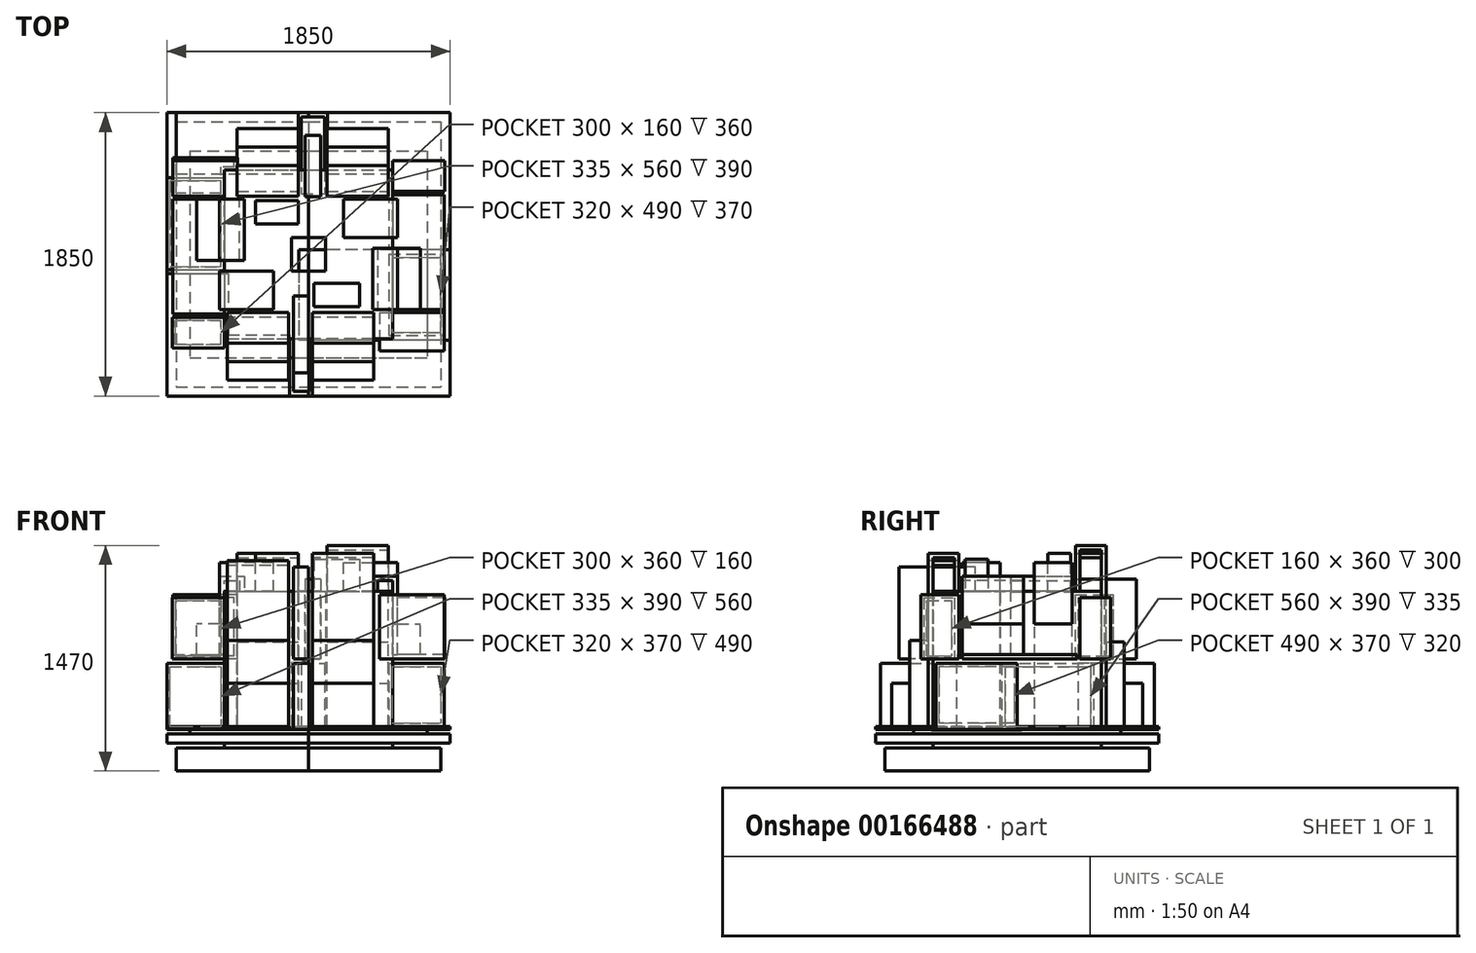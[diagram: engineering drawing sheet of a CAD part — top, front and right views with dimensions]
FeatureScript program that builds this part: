
annotation { "Feature Type Name" : "Feature", "Feature Type Description" : "" }
export const myFeature = defineFeature(function(context is Context, id is Id, definition is map)
    precondition{}
    {
        {
            var Q0;
            Q0=qCreatedBy(makeId("Top.planeOp"),FACE);
            var sketch = newSketch(context, id + "F0", { "sketchPlane" : qUnion([Q0])});
            skLineSegment(sketch, "E0.bottom", {"start": v(-865, 865) * mm, "end": v(865, 865) * mm});
            skLineSegment(sketch, "E0.top", {"start": v(-865, -865) * mm, "end": v(865, -865) * mm});
            skLineSegment(sketch, "E0.left", {"start": v(-865, 865) * mm, "end": v(-865, -865) * mm});
            skLineSegment(sketch, "E0.right", {"start": v(865, 865) * mm, "end": v(865, -865) * mm});
            skPoint(sketch, "E0.middle", {"position": v(0, 0) * mm});
            skSolve(sketch);
        }
        {
            var Q0;
            Q0 = qSketchRegion(id + "F0", true);
            extrude(context, id + "F1", {"entities" : qUnion([Q0]), "depth" : 150 * mm});
        }
        {
            var Q0;
            Q0=makeQuery(id+"F1.opExtrude","CAP_FACE",FACE,{"disambiguationData":[OSD([sQuery(id+"F0.wireOp",EDGE,"E0.bottom"),sQuery(id+"F0.wireOp",EDGE,"E0.top"),sQuery(id+"F0.wireOp",EDGE,"E0.left"),sQuery(id+"F0.wireOp",EDGE,"E0.right")])],"isStart":false});
            var sketch = newSketch(context, id + "F2", { "sketchPlane" : qUnion([Q0])});
            skLineSegment(sketch, "E1.bottom", {"start": v(-550, 550) * mm, "end": v(550, 550) * mm});
            skLineSegment(sketch, "E1.top", {"start": v(-550, -550) * mm, "end": v(550, -550) * mm});
            skLineSegment(sketch, "E1.left", {"start": v(-550, 550) * mm, "end": v(-550, -550) * mm});
            skLineSegment(sketch, "E1.right", {"start": v(550, 550) * mm, "end": v(550, -550) * mm});
            skPoint(sketch, "E1.middle", {"position": v(0, 0) * mm});
            skSolve(sketch);
        }
        {
            var Q0;
            Q0 = qSketchRegion(id + "F2", true);
            extrude(context, id + "F3", {"entities" : qUnion([Q0]), "depth" : 30 * mm});
        }
        {
            var Q0;
            Q0=makeQuery(id+"F3.opExtrude","CAP_FACE",FACE,{"disambiguationData":[OSD([sQuery(id+"F2.wireOp",EDGE,"E1.bottom"),sQuery(id+"F2.wireOp",EDGE,"E1.top"),sQuery(id+"F2.wireOp",EDGE,"E1.left"),sQuery(id+"F2.wireOp",EDGE,"E1.right")])],"isStart":false});
            var sketch = newSketch(context, id + "F4", { "sketchPlane" : qUnion([Q0])});
            skLineSegment(sketch, "E2.bottom", {"start": v(-925, 925) * mm, "end": v(925, 925) * mm});
            skLineSegment(sketch, "E2.top", {"start": v(-925, -925) * mm, "end": v(925, -925) * mm});
            skLineSegment(sketch, "E2.left", {"start": v(-925, 925) * mm, "end": v(-925, -925) * mm});
            skLineSegment(sketch, "E2.right", {"start": v(925, 925) * mm, "end": v(925, -925) * mm});
            skPoint(sketch, "E2.middle", {"position": v(0, 0) * mm});
            skSolve(sketch);
        }
        {
            var Q0;
            Q0 = qSketchRegion(id + "F4", true);
            extrude(context, id + "F5", {"entities" : qUnion([Q0]), "depth" : 60 * mm});
        }
        {
            var Q0;
            Q0=makeQuery(id+"F5.opExtrude","CAP_FACE",FACE,{"disambiguationData":[OSD([sQuery(id+"F4.wireOp",EDGE,"E2.bottom"),sQuery(id+"F4.wireOp",EDGE,"E2.top"),sQuery(id+"F4.wireOp",EDGE,"E2.left"),sQuery(id+"F4.wireOp",EDGE,"E2.right")])],"isStart":false});
            var sketch = newSketch(context, id + "F6", { "sketchPlane" : qUnion([Q0])});
            skLineSegment(sketch, "E3.bottom", {"start": v(-775, 674.89) * mm, "end": v(775, 674.89) * mm});
            skLineSegment(sketch, "E3.top", {"start": v(-775, -674.89) * mm, "end": v(775, -674.89) * mm});
            skLineSegment(sketch, "E3.left", {"start": v(-775, 674.89) * mm, "end": v(-775, -674.89) * mm});
            skLineSegment(sketch, "E3.right", {"start": v(775, 674.89) * mm, "end": v(775, -674.89) * mm});
            skPoint(sketch, "E3.middle", {"position": v(0, 0) * mm});
            skSolve(sketch);
        }
        {
            var Q0;
            Q0=makeQuery(id+"F6.imprint","IMPRINT",FACE,{"disambiguationData":[TD([[makeQuery(id+"F6.imprint","IMPRINT",EDGE,{"derivedFrom":sQuery(id+"F6.wireOp",EDGE,"E3.bottom")}),-1.0]])]});
            extrude(context, id + "F7", {"entities" : qUnion([Q0]), "depth" : 30 * mm});
        }
        {
            var Q0;
            Q0=makeQuery(id+"F7.opExtrude","CAP_FACE",FACE,{"disambiguationData":[OSD([sQuery(id+"F6.wireOp",EDGE,"E3.bottom"),sQuery(id+"F6.wireOp",EDGE,"E3.top"),sQuery(id+"F6.wireOp",EDGE,"E3.left"),sQuery(id+"F6.wireOp",EDGE,"E3.right")])],"isStart":false});
            var sketch = newSketch(context, id + "F8", { "sketchPlane" : qUnion([Q0])});
            skLineSegment(sketch, "E4.0", {"start": v(-925, -125) * mm, "end": v(-925, -925) * mm});
            skLineSegment(sketch, "E4.1", {"start": v(-925, -925) * mm, "end": v(-125, -925) * mm});
            skLineSegment(sketch, "E4.2", {"start": v(925, 925) * mm, "end": v(925, 25) * mm});
            skLineSegment(sketch, "E4.3", {"start": v(-865, 925) * mm, "end": v(-65, 925) * mm});
            skLineSegment(sketch, "E5", {"start": v(-925, -125) * mm, "end": v(-525, -125) * mm});
            skLineSegment(sketch, "E6", {"start": v(-525, -125) * mm, "end": v(-525, -525) * mm});
            skLineSegment(sketch, "E7", {"start": v(-525, -525) * mm, "end": v(-125, -525) * mm});
            skLineSegment(sketch, "E8", {"start": v(-125, -525) * mm, "end": v(-125, -925) * mm});
            skLineSegment(sketch, "E9", {"start": v(925, -525) * mm, "end": v(25, -525) * mm});
            skLineSegment(sketch, "E10", {"start": v(25, -525) * mm, "end": v(25, -925) * mm});
            skLineSegment(sketch, "E11", {"start": v(-865, 925) * mm, "end": v(-865, 525) * mm});
            skLineSegment(sketch, "E12", {"start": v(-865, 525) * mm, "end": v(-65, 525) * mm});
            skLineSegment(sketch, "E13", {"start": v(-65, 525) * mm, "end": v(-65, 925) * mm});
            skLineSegment(sketch, "E14", {"start": v(125, 925) * mm, "end": v(125, 525) * mm});
            skLineSegment(sketch, "E15", {"start": v(125, 525) * mm, "end": v(525, 525) * mm});
            skLineSegment(sketch, "E16", {"start": v(525, 525) * mm, "end": v(525, 25) * mm});
            skLineSegment(sketch, "E17.trimOffspring", {"start": v(925, -525) * mm, "end": v(925, -925) * mm});
            skLineSegment(sketch, "E18", {"start": v(925, 25) * mm, "end": v(525, 25) * mm});
            skLineSegment(sketch, "E19.trimOffspring", {"start": v(125, 925) * mm, "end": v(925, 925) * mm});
            skPoint(sketch, "E20.orphan", {"position": v(-925, 925) * mm});
            skLineSegment(sketch, "E21.trimOffspring", {"start": v(25, -925) * mm, "end": v(925, -925) * mm});
            skSolve(sketch);
        }
        {
            var Q0;
            Q0 = qSketchRegion(id + "F8", true);
            extrude(context, id + "F9", {"entities" : qUnion([Q0]), "depth" : 20 * mm});
        }
        {
            var Q0;
            Q0=makeQuery(id+"F7.opExtrude","CAP_FACE",FACE,{"disambiguationData":[OSD([sQuery(id+"F6.wireOp",EDGE,"E3.bottom"),sQuery(id+"F6.wireOp",EDGE,"E3.top"),sQuery(id+"F6.wireOp",EDGE,"E3.left"),sQuery(id+"F6.wireOp",EDGE,"E3.right")])],"isStart":false});
            var sketch = newSketch(context, id + "F10", { "sketchPlane" : qUnion([Q0])});
            skLineSegment(sketch, "E22", {"start": v(-49.02, -922.35) * mm, "end": v(-49.02, -892.35) * mm, "construction": true});
            skLineSegment(sketch, "E23", {"start": v(-127.92, -892.35) * mm, "end": v(-97.92, -892.35) * mm, "construction": true});
            skLineSegment(sketch, "E24.bottom", {"start": v(-97.92, -892.35) * mm, "end": v(2.08, -892.35) * mm});
            skLineSegment(sketch, "E24.top", {"start": v(-97.92, -392.35) * mm, "end": v(2.08, -392.35) * mm});
            skLineSegment(sketch, "E24.left", {"start": v(-97.92, -892.35) * mm, "end": v(-97.92, -392.35) * mm});
            skLineSegment(sketch, "E24.right", {"start": v(2.08, -892.35) * mm, "end": v(2.08, -392.35) * mm});
            skLineSegment(sketch, "E25", {"start": v(0, 926.82) * mm, "end": v(0, 896.82) * mm, "construction": true});
            skLineSegment(sketch, "E26", {"start": v(-66.36, 896.82) * mm, "end": v(-46.36, 896.82) * mm});
            skLineSegment(sketch, "E27.bottom", {"start": v(-46.36, 896.82) * mm, "end": v(103.64, 896.82) * mm});
            skLineSegment(sketch, "E27.top", {"start": v(-46.36, 396.82) * mm, "end": v(103.64, 396.82) * mm});
            skLineSegment(sketch, "E27.left", {"start": v(-46.36, 896.82) * mm, "end": v(-46.36, 396.82) * mm});
            skLineSegment(sketch, "E27.right", {"start": v(103.64, 896.82) * mm, "end": v(103.64, 396.82) * mm});
            skLineSegment(sketch, "E28.bottom", {"start": v(-925, -100) * mm, "end": v(-525, -100) * mm});
            skLineSegment(sketch, "E28.top", {"start": v(-925, 500) * mm, "end": v(-525, 500) * mm});
            skLineSegment(sketch, "E28.left", {"start": v(-925, -100) * mm, "end": v(-925, 500) * mm});
            skLineSegment(sketch, "E28.right", {"start": v(-525, -100) * mm, "end": v(-525, 500) * mm});
            skLineSegment(sketch, "E29", {"start": v(-861.36, 547.89) * mm, "end": v(-861.36, 500) * mm, "construction": true});
            skLineSegment(sketch, "E30.bottom", {"start": v(524.84, 0) * mm, "end": v(884.84, 0) * mm});
            skLineSegment(sketch, "E30.top", {"start": v(524.84, -530) * mm, "end": v(884.84, -530) * mm});
            skLineSegment(sketch, "E30.left", {"start": v(524.84, 0) * mm, "end": v(524.84, -530) * mm});
            skLineSegment(sketch, "E30.right", {"start": v(884.84, 0) * mm, "end": v(884.84, -530) * mm});
            skLineSegment(sketch, "E31", {"start": v(524.84, 0) * mm, "end": v(524.84, 30) * mm, "construction": true});
            skLineSegment(sketch, "E32", {"start": v(524.84, -530) * mm, "end": v(524.84, -560) * mm});
            skSolve(sketch);
        }
        {
            var Q0;
            Q0 = qSketchRegion(id + "F10", true);
            extrude(context, id + "F11", {"entities" : qUnion([Q0]), "depth" : 430 * mm});
        }
        {
            var Q0;
            Q0=makeQuery(id+"F7.opExtrude","CAP_FACE",FACE,{"disambiguationData":[OSD([sQuery(id+"F6.wireOp",EDGE,"E3.bottom"),sQuery(id+"F6.wireOp",EDGE,"E3.top"),sQuery(id+"F6.wireOp",EDGE,"E3.left"),sQuery(id+"F6.wireOp",EDGE,"E3.right")])],"isStart":false});
            var sketch = newSketch(context, id + "F12", { "sketchPlane" : qUnion([Q0])});
            skLineSegment(sketch, "E33.bottom", {"start": v(-550, 550) * mm, "end": v(550, 550) * mm});
            skLineSegment(sketch, "E33.top", {"start": v(-550, -550) * mm, "end": v(550, -550) * mm});
            skLineSegment(sketch, "E33.left", {"start": v(-550, 550) * mm, "end": v(-550, -550) * mm});
            skLineSegment(sketch, "E33.right", {"start": v(550, 550) * mm, "end": v(550, -550) * mm});
            skPoint(sketch, "E33.middle", {"position": v(0, 0) * mm});
            skLineSegment(sketch, "E34.bottom", {"start": v(-110, 110) * mm, "end": v(110, 110) * mm});
            skLineSegment(sketch, "E34.top", {"start": v(-110, -110) * mm, "end": v(110, -110) * mm});
            skLineSegment(sketch, "E34.left", {"start": v(-110, 110) * mm, "end": v(-110, -110) * mm});
            skLineSegment(sketch, "E34.right", {"start": v(110, 110) * mm, "end": v(110, -110) * mm});
            skSolve(sketch);
        }
        {
            var Q0;
            Q0 = qSketchRegion(id + "F12", true);
            extrude(context, id + "F13", {"entities" : qUnion([Q0]), "depth" : 900 * mm});
        }
        {
            var Q0;
            Q0=makeQuery(id+"F13.opExtrude","SWEPT_FACE",FACE,{"disambiguationData":[OSD([sQuery(id+"F12.wireOp",EDGE,"E33.left")])]});
            cPlane(context, id + "F14", {"entities" : qUnion([Q0]), "cplaneType" : CPlaneType.OFFSET, "offset" : 20 * mm, "oppositeDirection" : true, "width" : 150 * mm, "height" : 150 * mm});
        }
        {
            var Q0;
            Q0=qCreatedBy(id+"F14.planeOp",FACE);
            var sketch = newSketch(context, id + "F15", { "sketchPlane" : qUnion([Q0])});
            skLineSegment(sketch, "E35.bottom", {"start": v(550, 290) * mm, "end": v(580, 290) * mm});
            skLineSegment(sketch, "E35.top", {"start": v(550, 1370) * mm, "end": v(580, 1370) * mm});
            skLineSegment(sketch, "E35.left", {"start": v(550, 290) * mm, "end": v(550, 1340) * mm});
            skLineSegment(sketch, "E35.right", {"start": v(580, 290) * mm, "end": v(580, 1370) * mm});
            skLineSegment(sketch, "E36.0", {"start": v(125, 290) * mm, "end": v(925, 290) * mm, "construction": true});
            skLineSegment(sketch, "E37.1", {"start": v(550, 1170) * mm, "end": v(550, 270) * mm, "construction": true});
            skLineSegment(sketch, "E38.bottom", {"start": v(550, 1370) * mm, "end": v(380, 1370) * mm});
            skLineSegment(sketch, "E38.top", {"start": v(550, 1340) * mm, "end": v(410, 1340) * mm});
            skLineSegment(sketch, "E38.right", {"start": v(380, 1370) * mm, "end": v(380, 1340) * mm});
            skLineSegment(sketch, "E39.bottom", {"start": v(380, 1370) * mm, "end": v(410, 1370) * mm});
            skLineSegment(sketch, "E39.top", {"start": v(380, 1170) * mm, "end": v(410, 1170) * mm});
            skLineSegment(sketch, "E39.left", {"start": v(380, 1340) * mm, "end": v(380, 1170) * mm});
            skLineSegment(sketch, "E39.right", {"start": v(410, 1340) * mm, "end": v(410, 1170) * mm});
            skLineSegment(sketch, "E40.0.1", {"start": v(550, 270) * mm, "end": v(550, 1170) * mm});
            skLineSegment(sketch, "E41.0.1", {"start": v(550, 270) * mm, "end": v(550, 1170) * mm, "construction": true});
            skSolve(sketch);
        }
        {
            var Q0;
            Q0 = qSketchRegion(id + "F15", true);
            extrude(context, id + "F16", {"entities" : qUnion([Q0]), "oppositeDirection" : true, "depth" : 400 * mm});
        }
        {
            var Q0;
            Q0=makeQuery(id+"F9.opExtrude","SWEPT_FACE",FACE,{"disambiguationData":[OSD([sQuery(id+"F8.wireOp",EDGE,"E10")])]});
            var sketch = newSketch(context, id + "F17", { "sketchPlane" : qUnion([Q0])});
            skLineSegment(sketch, "E42.bottom", {"start": v(380, 1170) * mm, "end": v(410, 1170) * mm});
            skLineSegment(sketch, "E42.left", {"start": v(380, 1170) * mm, "end": v(380, 1420) * mm});
            skLineSegment(sketch, "E43", {"start": v(380, 1420) * mm, "end": v(580, 1420) * mm});
            skLineSegment(sketch, "E44", {"start": v(580, 1420) * mm, "end": v(580, 290) * mm});
            skLineSegment(sketch, "E45.0", {"start": v(550, 1390) * mm, "end": v(550, 290) * mm});
            skLineSegment(sketch, "E45.1", {"start": v(410, 1390) * mm, "end": v(550, 1390) * mm});
            skLineSegment(sketch, "E45.2", {"start": v(410, 1170) * mm, "end": v(410, 1390) * mm});
            skLineSegment(sketch, "E46", {"start": v(580, 290) * mm, "end": v(550, 290) * mm});
            skSolve(sketch);
        }
        {
            var Q0;
            Q0 = qSketchRegion(id + "F17", true);
            extrude(context, id + "F18", {"entities" : qUnion([Q0]), "oppositeDirection" : true, "depth" : 400 * mm});
        }
        {
            var Q0;
            Q0=makeQuery(id+"F13.opExtrude","SWEPT_FACE",FACE,{"disambiguationData":[OSD([sQuery(id+"F12.wireOp",EDGE,"E33.right")])]});
            cPlane(context, id + "F19", {"entities" : qUnion([Q0]), "cplaneType" : CPlaneType.OFFSET, "offset" : 30 * mm, "oppositeDirection" : true, "width" : 150 * mm, "height" : 150 * mm});
        }
        {
            var Q0;
            Q0=qCreatedBy(id+"F19.planeOp",FACE);
            var sketch = newSketch(context, id + "F20", { "sketchPlane" : qUnion([Q0])});
            skLineSegment(sketch, "E47", {"start": v(550, 290) * mm, "end": v(580, 290) * mm});
            skLineSegment(sketch, "E48", {"start": v(580, 290) * mm, "end": v(580, 1470) * mm});
            skLineSegment(sketch, "E49", {"start": v(580, 1470) * mm, "end": v(380, 1470) * mm});
            skLineSegment(sketch, "E50", {"start": v(380, 1470) * mm, "end": v(380, 1170) * mm});
            skLineSegment(sketch, "E51.0", {"start": v(410, 1440) * mm, "end": v(410, 1170) * mm});
            skLineSegment(sketch, "E51.1", {"start": v(550, 1440) * mm, "end": v(410, 1440) * mm});
            skLineSegment(sketch, "E51.2", {"start": v(550, 290) * mm, "end": v(550, 1440) * mm});
            skLineSegment(sketch, "E52", {"start": v(380, 1170) * mm, "end": v(410, 1170) * mm});
            skSolve(sketch);
        }
        {
            var Q0;
            Q0 = qSketchRegion(id + "F20", true);
            var Q1;
            Q1=makeQuery(id+"F9.opExtrude","SWEPT_FACE",FACE,{"disambiguationData":[OSD([sQuery(id+"F8.wireOp",EDGE,"E14")])]});
            extrude(context, id + "F21", {"entities" : qUnion([Q0]), "oppositeDirection" : true, "endBoundEntityFace" : qUnion([Q1]), "depth" : 400 * mm});
        }
        {
            var Q0;
            Q0=makeQuery(id+"F9.opExtrude","SWEPT_FACE",FACE,{"disambiguationData":[OSD([sQuery(id+"F8.wireOp",EDGE,"E13")])]});
            var sketch = newSketch(context, id + "F22", { "sketchPlane" : qUnion([Q0])});
            skLineSegment(sketch, "E53.0.1", {"start": v(550, 290) * mm, "end": v(580, 290) * mm});
            skLineSegment(sketch, "E53.0.2", {"start": v(580, 290) * mm, "end": v(580, 1420) * mm});
            skLineSegment(sketch, "E53.0.4", {"start": v(380, 1420) * mm, "end": v(380, 1170) * mm});
            skLineSegment(sketch, "E53.0.5", {"start": v(380, 1170) * mm, "end": v(410, 1170) * mm});
            skLineSegment(sketch, "E53.0.6", {"start": v(410, 1170) * mm, "end": v(410, 1390) * mm});
            skLineSegment(sketch, "E54", {"start": v(380, 1420) * mm, "end": v(580, 1420) * mm});
            skLineSegment(sketch, "E55", {"start": v(410, 1390) * mm, "end": v(550, 1390) * mm});
            skPoint(sketch, "E56.orphan", {"position": v(380, 1470) * mm});
            skPoint(sketch, "E57.orphan", {"position": v(580, 1470) * mm});
            skLineSegment(sketch, "E58.trimOffspring", {"start": v(550, 1390) * mm, "end": v(550, 290) * mm});
            skPoint(sketch, "E53.0.0.start.orphan", {"position": v(550, 1440) * mm});
            skPoint(sketch, "E59.orphan", {"position": v(410, 1440) * mm});
            skSolve(sketch);
        }
        {
            var Q0;
            Q0 = qSketchRegion(id + "F22", true);
            extrude(context, id + "F23", {"entities" : qUnion([Q0]), "oppositeDirection" : true, "depth" : 400 * mm});
        }
        {
            var Q0;
            Q0=qCreatedBy(id+"F19.planeOp",FACE);
            var sketch = newSketch(context, id + "F24", { "sketchPlane" : qUnion([Q0])});
            skLineSegment(sketch, "E60.bottom", {"start": v(580, 290) * mm, "end": v(700, 290) * mm});
            skLineSegment(sketch, "E60.top", {"start": v(580, 840) * mm, "end": v(700, 840) * mm});
            skLineSegment(sketch, "E60.left", {"start": v(580, 290) * mm, "end": v(580, 840) * mm});
            skLineSegment(sketch, "E60.right", {"start": v(700, 290) * mm, "end": v(700, 840) * mm});
            skSolve(sketch);
        }
        {
            var Q0;
            Q0 = qSketchRegion(id + "F24", true);
            var Q1;
            Q1=makeQuery(id+"F21.opExtrude","CAP_FACE",FACE,{"disambiguationData":[OSD([sQuery(id+"F8.wireOp",EDGE,"E14")])],"isStart":false});
            extrude(context, id + "F25", {"entities" : qUnion([Q0]), "oppositeDirection" : true, "endBoundEntityFace" : qUnion([Q1]), "depth" : 400 * mm});
        }
        {
            var Q0;
            Q0=qCreatedBy(id+"F19.planeOp",FACE);
            var sketch = newSketch(context, id + "F26", { "sketchPlane" : qUnion([Q0])});
            skLineSegment(sketch, "E61.bottom", {"start": v(700, 290) * mm, "end": v(820, 290) * mm});
            skLineSegment(sketch, "E61.top", {"start": v(700, 570) * mm, "end": v(820, 570) * mm});
            skLineSegment(sketch, "E61.left", {"start": v(700, 290) * mm, "end": v(700, 570) * mm});
            skLineSegment(sketch, "E61.right", {"start": v(820, 290) * mm, "end": v(820, 570) * mm});
            skSolve(sketch);
        }
        {
            var Q0;
            Q0 = qSketchRegion(id + "F26", true);
            var Q1;
            Q1=makeQuery(id+"F25.opExtrude","CAP_FACE",FACE,{"disambiguationData":[OSD([sQuery(id+"F8.wireOp",EDGE,"E14")])],"isStart":false});
            extrude(context, id + "F27", {"entities" : qUnion([Q0]), "oppositeDirection" : true, "endBoundEntityFace" : qUnion([Q1]), "depth" : 400 * mm});
        }
        {
            var Q0;
            Q0=makeQuery(id+"F23.opExtrude","CAP_FACE",FACE,{"disambiguationData":[OSD([sQuery(id+"F22.wireOp",EDGE,"E53.0.1"),sQuery(id+"F22.wireOp",EDGE,"E53.0.2"),sQuery(id+"F22.wireOp",EDGE,"E53.0.4"),sQuery(id+"F22.wireOp",EDGE,"E53.0.5"),sQuery(id+"F22.wireOp",EDGE,"E53.0.6"),sQuery(id+"F22.wireOp",EDGE,"E54"),sQuery(id+"F22.wireOp",EDGE,"E55"),sQuery(id+"F22.wireOp",EDGE,"E58.trimOffspring")])],"isStart":true});
            var sketch = newSketch(context, id + "F28", { "sketchPlane" : qUnion([Q0])});
            skLineSegment(sketch, "E62.0.0", {"start": v(580, 840) * mm, "end": v(580, 290) * mm});
            skLineSegment(sketch, "E62.0.1", {"start": v(580, 290) * mm, "end": v(700, 290) * mm});
            skLineSegment(sketch, "E62.0.2", {"start": v(700, 290) * mm, "end": v(700, 840) * mm});
            skLineSegment(sketch, "E62.0.3", {"start": v(700, 840) * mm, "end": v(580, 840) * mm});
            skSolve(sketch);
        }
        {
            var Q0;
            Q0 = qSketchRegion(id + "F28", true);
            var Q1;
            Q1=makeQuery(id+"F23.opExtrude","CAP_FACE",FACE,{"disambiguationData":[OSD([sQuery(id+"F22.wireOp",EDGE,"E53.0.1"),sQuery(id+"F22.wireOp",EDGE,"E53.0.2"),sQuery(id+"F22.wireOp",EDGE,"E53.0.4"),sQuery(id+"F22.wireOp",EDGE,"E53.0.5"),sQuery(id+"F22.wireOp",EDGE,"E53.0.6"),sQuery(id+"F22.wireOp",EDGE,"E54"),sQuery(id+"F22.wireOp",EDGE,"E55"),sQuery(id+"F22.wireOp",EDGE,"E58.trimOffspring")])],"isStart":false});
            extrude(context, id + "F29", {"entities" : qUnion([Q0]), "endBound" : BoundingType.UP_TO_SURFACE, "oppositeDirection" : true, "endBoundEntityFace" : qUnion([Q1]), "depth" : 25 * mm});
        }
        {
            var Q0;
            Q0=makeQuery(id+"F29.opExtrude","CAP_FACE",FACE,{"disambiguationData":[OSD([sQuery(id+"F28.wireOp",EDGE,"E62.0.0"),sQuery(id+"F28.wireOp",EDGE,"E62.0.1"),sQuery(id+"F28.wireOp",EDGE,"E62.0.2"),sQuery(id+"F28.wireOp",EDGE,"E62.0.3")])],"isStart":true});
            var sketch = newSketch(context, id + "F30", { "sketchPlane" : qUnion([Q0])});
            skLineSegment(sketch, "E63.0.0", {"start": v(700, 570) * mm, "end": v(700, 290) * mm});
            skLineSegment(sketch, "E63.0.1", {"start": v(700, 290) * mm, "end": v(820, 290) * mm});
            skLineSegment(sketch, "E63.0.2", {"start": v(820, 290) * mm, "end": v(820, 570) * mm});
            skLineSegment(sketch, "E63.0.3", {"start": v(820, 570) * mm, "end": v(700, 570) * mm});
            skSolve(sketch);
        }
        {
            var Q0;
            Q0 = qSketchRegion(id + "F30", true);
            var Q1;
            Q1=makeQuery(id+"F29.opExtrude","CAP_FACE",FACE,{"disambiguationData":[OSD([sQuery(id+"F28.wireOp",EDGE,"E62.0.0"),sQuery(id+"F28.wireOp",EDGE,"E62.0.1"),sQuery(id+"F28.wireOp",EDGE,"E62.0.2"),sQuery(id+"F28.wireOp",EDGE,"E62.0.3")])],"isStart":false});
            extrude(context, id + "F31", {"entities" : qUnion([Q0]), "endBound" : BoundingType.UP_TO_SURFACE, "oppositeDirection" : true, "endBoundEntityFace" : qUnion([Q1]), "depth" : 25 * mm});
        }
        {
            var Q0;
            Q0=makeQuery(id+"F18.opExtrude","CAP_FACE",FACE,{"disambiguationData":[OSD([sQuery(id+"F17.wireOp",EDGE,"E42.bottom"),sQuery(id+"F17.wireOp",EDGE,"E42.left"),sQuery(id+"F17.wireOp",EDGE,"E43"),sQuery(id+"F17.wireOp",EDGE,"E44"),sQuery(id+"F17.wireOp",EDGE,"E45.0"),sQuery(id+"F17.wireOp",EDGE,"E45.1"),sQuery(id+"F17.wireOp",EDGE,"E45.2"),sQuery(id+"F17.wireOp",EDGE,"E46")])],"isStart":false});
            var sketch = newSketch(context, id + "F32", { "sketchPlane" : qUnion([Q0])});
            skLineSegment(sketch, "E64.bottom", {"start": v(-580, 290) * mm, "end": v(-700, 290) * mm});
            skLineSegment(sketch, "E64.top", {"start": v(-580, 850) * mm, "end": v(-700, 850) * mm});
            skLineSegment(sketch, "E64.left", {"start": v(-580, 290) * mm, "end": v(-580, 850) * mm});
            skLineSegment(sketch, "E64.right", {"start": v(-700, 290) * mm, "end": v(-700, 850) * mm});
            skSolve(sketch);
        }
        {
            var Q0;
            Q0 = qSketchRegion(id + "F32", true);
            var Q1;
            Q1=makeQuery(id+"F18.opExtrude","CAP_FACE",FACE,{"disambiguationData":[OSD([sQuery(id+"F17.wireOp",EDGE,"E42.bottom"),sQuery(id+"F17.wireOp",EDGE,"E42.left"),sQuery(id+"F17.wireOp",EDGE,"E43"),sQuery(id+"F17.wireOp",EDGE,"E44"),sQuery(id+"F17.wireOp",EDGE,"E45.0"),sQuery(id+"F17.wireOp",EDGE,"E45.1"),sQuery(id+"F17.wireOp",EDGE,"E45.2"),sQuery(id+"F17.wireOp",EDGE,"E46")])],"isStart":true});
            extrude(context, id + "F33", {"entities" : qUnion([Q0]), "endBound" : BoundingType.UP_TO_SURFACE, "oppositeDirection" : true, "endBoundEntityFace" : qUnion([Q1]), "depth" : 25 * mm});
        }
        {
            var Q0;
            Q0=makeQuery(id+"F33.opExtrude","CAP_FACE",FACE,{"disambiguationData":[OSD([sQuery(id+"F32.wireOp",EDGE,"E64.bottom"),sQuery(id+"F32.wireOp",EDGE,"E64.top"),sQuery(id+"F32.wireOp",EDGE,"E64.left"),sQuery(id+"F32.wireOp",EDGE,"E64.right")])],"isStart":true});
            var sketch = newSketch(context, id + "F34", { "sketchPlane" : qUnion([Q0])});
            skLineSegment(sketch, "E65.bottom", {"start": v(-700, 290) * mm, "end": v(-820, 290) * mm});
            skLineSegment(sketch, "E65.top", {"start": v(-700, 570) * mm, "end": v(-820, 570) * mm});
            skLineSegment(sketch, "E65.left", {"start": v(-700, 290) * mm, "end": v(-700, 570) * mm});
            skLineSegment(sketch, "E65.right", {"start": v(-820, 290) * mm, "end": v(-820, 570) * mm});
            skSolve(sketch);
        }
        {
            var Q0;
            Q0 = qSketchRegion(id + "F34", true);
            var Q1;
            Q1=makeQuery(id+"F33.opExtrude","CAP_FACE",FACE,{"disambiguationData":[OSD([sQuery(id+"F32.wireOp",EDGE,"E64.bottom"),sQuery(id+"F32.wireOp",EDGE,"E64.top"),sQuery(id+"F32.wireOp",EDGE,"E64.left"),sQuery(id+"F32.wireOp",EDGE,"E64.right")])],"isStart":false});
            extrude(context, id + "F35", {"entities" : qUnion([Q0]), "endBound" : BoundingType.UP_TO_SURFACE, "oppositeDirection" : true, "endBoundEntityFace" : qUnion([Q1]), "depth" : 25 * mm});
        }
        {
            var Q0;
            Q0=makeQuery(id+"F16.opExtrude","CAP_FACE",FACE,{"disambiguationData":[OSD([sQuery(id+"F15.wireOp",EDGE,"E35.bottom"),sQuery(id+"F15.wireOp",EDGE,"E35.top"),sQuery(id+"F15.wireOp",EDGE,"E35.left"),sQuery(id+"F15.wireOp",EDGE,"E35.right"),sQuery(id+"F15.wireOp",EDGE,"E38.bottom"),sQuery(id+"F15.wireOp",EDGE,"E38.top"),sQuery(id+"F15.wireOp",EDGE,"E38.right"),sQuery(id+"F15.wireOp",EDGE,"E39.bottom"),sQuery(id+"F15.wireOp",EDGE,"E39.top"),sQuery(id+"F15.wireOp",EDGE,"E39.left"),sQuery(id+"F15.wireOp",EDGE,"E39.right"),sQuery(id+"F15.wireOp",EDGE,"E40.0.1")])],"isStart":false});
            var sketch = newSketch(context, id + "F36", { "sketchPlane" : qUnion([Q0])});
            skLineSegment(sketch, "E66.0.0", {"start": v(-700, 290) * mm, "end": v(-580, 290) * mm});
            skLineSegment(sketch, "E66.0.1", {"start": v(-580, 290) * mm, "end": v(-580, 850) * mm});
            skLineSegment(sketch, "E66.0.2", {"start": v(-580, 850) * mm, "end": v(-700, 850) * mm});
            skLineSegment(sketch, "E66.0.3", {"start": v(-700, 850) * mm, "end": v(-700, 290) * mm});
            skSolve(sketch);
        }
        {
            var Q0;
            Q0 = qSketchRegion(id + "F36", true);
            var Q1;
            Q1=makeQuery(id+"F16.opExtrude","CAP_FACE",FACE,{"disambiguationData":[OSD([sQuery(id+"F15.wireOp",EDGE,"E35.bottom"),sQuery(id+"F15.wireOp",EDGE,"E35.top"),sQuery(id+"F15.wireOp",EDGE,"E35.left"),sQuery(id+"F15.wireOp",EDGE,"E35.right"),sQuery(id+"F15.wireOp",EDGE,"E38.bottom"),sQuery(id+"F15.wireOp",EDGE,"E38.top"),sQuery(id+"F15.wireOp",EDGE,"E38.right"),sQuery(id+"F15.wireOp",EDGE,"E39.bottom"),sQuery(id+"F15.wireOp",EDGE,"E39.top"),sQuery(id+"F15.wireOp",EDGE,"E39.left"),sQuery(id+"F15.wireOp",EDGE,"E39.right"),sQuery(id+"F15.wireOp",EDGE,"E40.0.1")])],"isStart":true});
            extrude(context, id + "F37", {"entities" : qUnion([Q0]), "endBound" : BoundingType.UP_TO_SURFACE, "oppositeDirection" : true, "endBoundEntityFace" : qUnion([Q1]), "depth" : 25 * mm});
        }
        {
            var Q0;
            Q0=makeQuery(id+"F37.opExtrude","CAP_FACE",FACE,{"disambiguationData":[OSD([sQuery(id+"F36.wireOp",EDGE,"E66.0.0"),sQuery(id+"F36.wireOp",EDGE,"E66.0.1"),sQuery(id+"F36.wireOp",EDGE,"E66.0.2"),sQuery(id+"F36.wireOp",EDGE,"E66.0.3")])],"isStart":true});
            var sketch = newSketch(context, id + "F38", { "sketchPlane" : qUnion([Q0])});
            skLineSegment(sketch, "E67.0.0", {"start": v(-820, 290) * mm, "end": v(-700, 290) * mm});
            skLineSegment(sketch, "E67.0.1", {"start": v(-700, 290) * mm, "end": v(-700, 570) * mm});
            skLineSegment(sketch, "E67.0.2", {"start": v(-700, 570) * mm, "end": v(-820, 570) * mm});
            skLineSegment(sketch, "E67.0.3", {"start": v(-820, 570) * mm, "end": v(-820, 290) * mm});
            skSolve(sketch);
        }
        {
            var Q0;
            Q0 = qSketchRegion(id + "F38", true);
            var Q1;
            Q1=makeQuery(id+"F37.opExtrude","CAP_FACE",FACE,{"disambiguationData":[OSD([sQuery(id+"F36.wireOp",EDGE,"E66.0.0"),sQuery(id+"F36.wireOp",EDGE,"E66.0.1"),sQuery(id+"F36.wireOp",EDGE,"E66.0.2"),sQuery(id+"F36.wireOp",EDGE,"E66.0.3")])],"isStart":false});
            extrude(context, id + "F39", {"entities" : qUnion([Q0]), "endBound" : BoundingType.UP_TO_SURFACE, "oppositeDirection" : true, "endBoundEntityFace" : qUnion([Q1]), "depth" : 171 * mm});
        }
        {
            var Q0;
            Q0=makeQuery(id+"F11.opExtrude","SWEPT_FACE",FACE,{"disambiguationData":[OSD([sQuery(id+"F10.wireOp",EDGE,"E24.bottom")])]});
            cPlane(context, id + "F40", {"entities" : qUnion([Q0]), "cplaneType" : CPlaneType.OFFSET, "offset" : 120 * mm, "oppositeDirection" : true, "width" : 150 * mm, "height" : 150 * mm});
        }
        {
            var Q0;
            Q0=qCreatedBy(id+"F40.planeOp",FACE);
            var sketch = newSketch(context, id + "F41", { "sketchPlane" : qUnion([Q0])});
            skLineSegment(sketch, "E68.0", {"start": v(-97.92, 700) * mm, "end": v(-97.92, 270) * mm, "construction": true});
            skLineSegment(sketch, "E68.1", {"start": v(2.08, 700) * mm, "end": v(2.08, 270) * mm, "construction": true});
            skLineSegment(sketch, "E69.bottom", {"start": v(-97.92, 730) * mm, "end": v(0, 730) * mm});
            skLineSegment(sketch, "E69.top", {"start": v(-97.92, 1330) * mm, "end": v(0, 1330) * mm});
            skLineSegment(sketch, "E69.left", {"start": v(-97.92, 730) * mm, "end": v(-97.92, 1330) * mm});
            skLineSegment(sketch, "E69.right", {"start": v(0, 730) * mm, "end": v(0, 1330) * mm});
            skSolve(sketch);
        }
        {
            var Q0;
            Q0 = qSketchRegion(id + "F41", true);
            extrude(context, id + "F42", {"entities" : qUnion([Q0]), "oppositeDirection" : true, "depth" : 500 * mm});
        }
        {
            var Q0;
            Q0=makeQuery(id+"F11.opExtrude","SWEPT_FACE",FACE,{"disambiguationData":[OSD([sQuery(id+"F10.wireOp",EDGE,"E27.bottom")])]});
            cPlane(context, id + "F43", {"entities" : qUnion([Q0]), "cplaneType" : CPlaneType.OFFSET, "offset" : 120 * mm, "oppositeDirection" : true, "width" : 150 * mm, "height" : 150 * mm});
        }
        {
            var Q0;
            Q0=qCreatedBy(id+"F43.planeOp",FACE);
            var sketch = newSketch(context, id + "F44", { "sketchPlane" : qUnion([Q0])});
            skLineSegment(sketch, "E70.0", {"start": v(46.36, 700) * mm, "end": v(-103.64, 700) * mm, "construction": true});
            skLineSegment(sketch, "E71", {"start": v(-28.64, 700) * mm, "end": v(-28.64, 1224.04) * mm, "construction": true});
            skLineSegment(sketch, "E72.bottom", {"start": v(-78.64, 1250) * mm, "end": v(21.36, 1250) * mm});
            skLineSegment(sketch, "E72.top", {"start": v(-78.64, 730) * mm, "end": v(21.36, 730) * mm});
            skLineSegment(sketch, "E72.left", {"start": v(-78.64, 1250) * mm, "end": v(-78.64, 730) * mm});
            skLineSegment(sketch, "E72.right", {"start": v(21.36, 1250) * mm, "end": v(21.36, 730) * mm});
            skPoint(sketch, "E72.middle", {"position": v(-28.64, 990) * mm});
            skSolve(sketch);
        }
        {
            var Q0;
            Q0 = qSketchRegion(id + "F44", true);
            extrude(context, id + "F45", {"entities" : qUnion([Q0]), "oppositeDirection" : true, "depth" : 400 * mm});
        }
        {
            var Q0;
            Q0=makeQuery(id+"F13.opExtrude","SWEPT_FACE",FACE,{"disambiguationData":[OSD([sQuery(id+"F12.wireOp",EDGE,"E33.right")])]});
            var sketch = newSketch(context, id + "F46", { "sketchPlane" : qUnion([Q0])});
            skLineSegment(sketch, "E73.bottom", {"start": v(-360, 760) * mm, "end": v(390, 760) * mm});
            skLineSegment(sketch, "E73.top", {"start": v(-360, 730) * mm, "end": v(390, 730) * mm});
            skLineSegment(sketch, "E73.left", {"start": v(-360, 760) * mm, "end": v(-360, 730) * mm});
            skLineSegment(sketch, "E73.right", {"start": v(390, 760) * mm, "end": v(390, 730) * mm});
            skSolve(sketch);
        }
        {
            var Q0;
            Q0 = qSketchRegion(id + "F46", true);
            var Q1;
            Q1=makeQuery(id+"F11.opExtrude","SWEPT_FACE",FACE,{"disambiguationData":[OSD([sQuery(id+"F10.wireOp",EDGE,"E30.right")])]});
            extrude(context, id + "F47", {"entities" : qUnion([Q0]), "endBound" : BoundingType.UP_TO_SURFACE, "endBoundEntityFace" : qUnion([Q1]), "depth" : 25 * mm});
        }
        {
            var Q0;
            Q0=makeQuery(id+"F47.opExtrude","SWEPT_FACE",FACE,{"disambiguationData":[OSD([sQuery(id+"F46.wireOp",EDGE,"E73.left")])]});
            var sketch = newSketch(context, id + "F48", { "sketchPlane" : qUnion([Q0])});
            skLineSegment(sketch, "E74.bottom", {"start": v(580, 760) * mm, "end": v(730, 760) * mm});
            skLineSegment(sketch, "E74.top", {"start": v(580, 960) * mm, "end": v(730, 960) * mm});
            skLineSegment(sketch, "E74.left", {"start": v(580, 760) * mm, "end": v(580, 960) * mm});
            skLineSegment(sketch, "E74.right", {"start": v(730, 760) * mm, "end": v(730, 960) * mm});
            skSolve(sketch);
        }
        {
            var Q0;
            Q0 = qSketchRegion(id + "F48", true);
            extrude(context, id + "F49", {"entities" : qUnion([Q0]), "oppositeDirection" : true, "depth" : 400 * mm});
        }
        {
            var Q0;
            Q0=makeQuery(id+"F49.opExtrude","CAP_FACE",FACE,{"disambiguationData":[OSD([sQuery(id+"F48.wireOp",EDGE,"E74.bottom"),sQuery(id+"F48.wireOp",EDGE,"E74.top"),sQuery(id+"F48.wireOp",EDGE,"E74.left"),sQuery(id+"F48.wireOp",EDGE,"E74.right")])],"isStart":true});
            var sketch = newSketch(context, id + "F50", { "sketchPlane" : qUnion([Q0])});
            skLineSegment(sketch, "E75", {"start": v(580, 760) * mm, "end": v(580, 1270) * mm});
            skLineSegment(sketch, "E76", {"start": v(580, 1270) * mm, "end": v(420, 1270) * mm});
            skLineSegment(sketch, "E77", {"start": v(420, 1270) * mm, "end": v(420, 1166.9) * mm});
            skLineSegment(sketch, "E78.0", {"start": v(450, 1240) * mm, "end": v(450, 1166.9) * mm});
            skLineSegment(sketch, "E78.1", {"start": v(550, 1240) * mm, "end": v(450, 1240) * mm});
            skLineSegment(sketch, "E78.2", {"start": v(550, 760) * mm, "end": v(550, 1240) * mm});
            skLineSegment(sketch, "E79", {"start": v(420, 1166.9) * mm, "end": v(450, 1166.9) * mm});
            skLineSegment(sketch, "E80", {"start": v(550, 760) * mm, "end": v(580, 760) * mm});
            skSolve(sketch);
        }
        {
            var Q0;
            Q0 = qSketchRegion(id + "F50", true);
            var Q1;
            Q1=makeQuery(id+"F49.opExtrude","CAP_FACE",FACE,{"disambiguationData":[OSD([sQuery(id+"F48.wireOp",EDGE,"E74.bottom"),sQuery(id+"F48.wireOp",EDGE,"E74.top"),sQuery(id+"F48.wireOp",EDGE,"E74.left"),sQuery(id+"F48.wireOp",EDGE,"E74.right")])],"isStart":false});
            extrude(context, id + "F51", {"entities" : qUnion([Q0]), "oppositeDirection" : true, "endBoundEntityFace" : qUnion([Q1]), "depth" : 400 * mm});
        }
        {
            var Q0;
            Q0=makeQuery(id+"F47.opExtrude","CAP_FACE",FACE,{"disambiguationData":[OSD([sQuery(id+"F46.wireOp",EDGE,"E73.bottom"),sQuery(id+"F46.wireOp",EDGE,"E73.top"),sQuery(id+"F46.wireOp",EDGE,"E73.left"),sQuery(id+"F46.wireOp",EDGE,"E73.right")])],"isStart":false});
            var sketch = newSketch(context, id + "F52", { "sketchPlane" : qUnion([Q0])});
            skLineSegment(sketch, "E81.bottom", {"start": v(-380, 730) * mm, "end": v(-630, 730) * mm});
            skLineSegment(sketch, "E81.top", {"start": v(-380, 1150) * mm, "end": v(-630, 1150) * mm});
            skLineSegment(sketch, "E81.left", {"start": v(-380, 730) * mm, "end": v(-380, 1150) * mm});
            skLineSegment(sketch, "E81.right", {"start": v(-630, 730) * mm, "end": v(-630, 1150) * mm});
            skSolve(sketch);
        }
        {
            var Q0;
            Q0 = qSketchRegion(id + "F52", true);
            extrude(context, id + "F53", {"entities" : qUnion([Q0]), "oppositeDirection" : true, "depth" : 420 * mm});
        }
        {
            var Q0;
            Q0=makeQuery(id+"F51.opExtrude","SWEPT_FACE",FACE,{"disambiguationData":[OSD([sQuery(id+"F50.wireOp",EDGE,"E75")])]});
            var sketch = newSketch(context, id + "F54", { "sketchPlane" : qUnion([Q0])});
            skLineSegment(sketch, "E82.bottom", {"start": v(110, 960) * mm, "end": v(360, 960) * mm});
            skLineSegment(sketch, "E82.top", {"start": v(110, 1360) * mm, "end": v(360, 1360) * mm});
            skLineSegment(sketch, "E82.left", {"start": v(110, 960) * mm, "end": v(110, 1360) * mm});
            skLineSegment(sketch, "E82.right", {"start": v(360, 960) * mm, "end": v(360, 1360) * mm});
            skSolve(sketch);
        }
        {
            var Q0;
            Q0 = qSketchRegion(id + "F54", true);
            extrude(context, id + "F55", {"entities" : qUnion([Q0]), "oppositeDirection" : true, "depth" : 350 * mm});
        }
        {
            var Q0;
            Q0=makeQuery(id+"F13.opExtrude","SWEPT_FACE",FACE,{"disambiguationData":[OSD([sQuery(id+"F12.wireOp",EDGE,"E33.right")])]});
            var sketch = newSketch(context, id + "F56", { "sketchPlane" : qUnion([Q0])});
            skLineSegment(sketch, "E83.bottom", {"start": v(610, 1130) * mm, "end": v(410, 1130) * mm});
            skLineSegment(sketch, "E83.top", {"start": v(610, 730) * mm, "end": v(410, 730) * mm});
            skLineSegment(sketch, "E83.left", {"start": v(610, 1130) * mm, "end": v(610, 730) * mm});
            skLineSegment(sketch, "E83.right", {"start": v(410, 1130) * mm, "end": v(410, 730) * mm});
            skSolve(sketch);
        }
        {
            var Q0;
            Q0 = qSketchRegion(id + "F56", true);
            extrude(context, id + "F57", {"entities" : qUnion([Q0]), "depth" : 340 * mm});
        }
        {
            var Q0;
            Q0=makeQuery(id+"F13.opExtrude","CAP_FACE",FACE,{"disambiguationData":[OSD([sQuery(id+"F12.wireOp",EDGE,"E33.bottom"),sQuery(id+"F12.wireOp",EDGE,"E33.top"),sQuery(id+"F12.wireOp",EDGE,"E33.left"),sQuery(id+"F12.wireOp",EDGE,"E33.right"),sQuery(id+"F12.wireOp",EDGE,"E34.bottom"),sQuery(id+"F12.wireOp",EDGE,"E34.top"),sQuery(id+"F12.wireOp",EDGE,"E34.left"),sQuery(id+"F12.wireOp",EDGE,"E34.right")])],"isStart":false});
            var sketch = newSketch(context, id + "F58", { "sketchPlane" : qUnion([Q0])});
            skLineSegment(sketch, "E84.bottom", {"start": v(35, -340) * mm, "end": v(335, -340) * mm});
            skLineSegment(sketch, "E84.top", {"start": v(35, -190) * mm, "end": v(335, -190) * mm});
            skLineSegment(sketch, "E84.left", {"start": v(35, -340) * mm, "end": v(35, -190) * mm});
            skLineSegment(sketch, "E84.right", {"start": v(335, -340) * mm, "end": v(335, -190) * mm});
            skSolve(sketch);
        }
        {
            var Q0;
            Q0 = qSketchRegion(id + "F58", true);
            extrude(context, id + "F59", {"entities" : qUnion([Q0]), "depth" : 210 * mm});
        }
        {
            var Q0;
            Q0=qCreatedBy(makeId("Front.planeOp"),FACE);
            var sketch = newSketch(context, id + "F60", { "sketchPlane" : qUnion([Q0])});
            skLineSegment(sketch, "E85", {"start": v(0, 0) * mm, "end": v(0, 1490.67) * mm, "construction": true});
            skSolve(sketch);
        }
        {
            var Q0;
            Q0=makeQuery(id+"F55.opExtrude","SWEPT_BODY",BODY,{"disambiguationData":[OSD([sQuery(id+"F54.wireOp",EDGE,"E82.bottom"),sQuery(id+"F54.wireOp",EDGE,"E82.top"),sQuery(id+"F54.wireOp",EDGE,"E82.left"),sQuery(id+"F54.wireOp",EDGE,"E82.right")])]});
            var Q1;
            Q1=makeQuery(id+"F51.opExtrude","SWEPT_BODY",BODY,{"disambiguationData":[OSD([sQuery(id+"F50.wireOp",EDGE,"E75"),sQuery(id+"F50.wireOp",EDGE,"E76"),sQuery(id+"F50.wireOp",EDGE,"E77"),sQuery(id+"F50.wireOp",EDGE,"E78.0"),sQuery(id+"F50.wireOp",EDGE,"E78.1"),sQuery(id+"F50.wireOp",EDGE,"E78.2"),sQuery(id+"F50.wireOp",EDGE,"E79"),sQuery(id+"F50.wireOp",EDGE,"E80")])]});
            var Q2;
            Q2=makeQuery(id+"F49.opExtrude","SWEPT_BODY",BODY,{"disambiguationData":[OSD([sQuery(id+"F48.wireOp",EDGE,"E74.bottom"),sQuery(id+"F48.wireOp",EDGE,"E74.top"),sQuery(id+"F48.wireOp",EDGE,"E74.left"),sQuery(id+"F48.wireOp",EDGE,"E74.right")])]});
            var Q3;
            Q3=makeQuery(id+"F53.opExtrude","SWEPT_BODY",BODY,{"disambiguationData":[OSD([sQuery(id+"F52.wireOp",EDGE,"E81.bottom"),sQuery(id+"F52.wireOp",EDGE,"E81.top"),sQuery(id+"F52.wireOp",EDGE,"E81.left"),sQuery(id+"F52.wireOp",EDGE,"E81.right")])]});
            var Q4;
            Q4=makeQuery(id+"F47.opExtrude","SWEPT_BODY",BODY,{"disambiguationData":[OSD([sQuery(id+"F46.wireOp",EDGE,"E73.bottom"),sQuery(id+"F46.wireOp",EDGE,"E73.top"),sQuery(id+"F46.wireOp",EDGE,"E73.left"),sQuery(id+"F46.wireOp",EDGE,"E73.right")])]});
            var Q5;
            Q5=makeQuery(id+"F57.opExtrude","SWEPT_BODY",BODY,{"disambiguationData":[OSD([sQuery(id+"F56.wireOp",EDGE,"E83.bottom"),sQuery(id+"F56.wireOp",EDGE,"E83.top"),sQuery(id+"F56.wireOp",EDGE,"E83.left"),sQuery(id+"F56.wireOp",EDGE,"E83.right")])]});
            var Q6;
            Q6=sQuery(id+"F60.wireOp",EDGE,"E85");
            circularPattern(context, id + "F61", {"entities" : qUnion([Q0, Q1, Q2, Q3, Q4, Q5]), "axis" : qUnion([Q6]), "angle" : 180 * degree, "instanceCount" : 2});
        }
        {
            var Q0;
            Q0=makeQuery(id+"F23.opExtrude","SWEPT_FACE",FACE,{"disambiguationData":[OSD([sQuery(id+"F22.wireOp",EDGE,"E54")])]});
            var sketch = newSketch(context, id + "F62", { "sketchPlane" : qUnion([Q0])});
            skLineSegment(sketch, "E86.bottom", {"start": v(-65, 350) * mm, "end": v(-345, 350) * mm});
            skLineSegment(sketch, "E86.top", {"start": v(-65, 200) * mm, "end": v(-345, 200) * mm});
            skLineSegment(sketch, "E86.left", {"start": v(-65, 350) * mm, "end": v(-65, 200) * mm});
            skLineSegment(sketch, "E86.right", {"start": v(-345, 350) * mm, "end": v(-345, 200) * mm});
            skSolve(sketch);
        }
        {
            var Q0;
            Q0 = qSketchRegion(id + "F62", true);
            var Q1;
            Q1=makeQuery(id+"F13.opExtrude","CAP_FACE",FACE,{"disambiguationData":[OSD([sQuery(id+"F12.wireOp",EDGE,"E33.bottom"),sQuery(id+"F12.wireOp",EDGE,"E33.top"),sQuery(id+"F12.wireOp",EDGE,"E33.left"),sQuery(id+"F12.wireOp",EDGE,"E33.right"),sQuery(id+"F12.wireOp",EDGE,"E34.bottom"),sQuery(id+"F12.wireOp",EDGE,"E34.top"),sQuery(id+"F12.wireOp",EDGE,"E34.left"),sQuery(id+"F12.wireOp",EDGE,"E34.right")])],"isStart":false});
            extrude(context, id + "F63", {"entities" : qUnion([Q0]), "endBound" : BoundingType.UP_TO_SURFACE, "oppositeDirection" : true, "endBoundEntityFace" : qUnion([Q1]), "depth" : 25 * mm});
        }
        {
            var Q0;
            Q0=makeQuery(id+"F13.opExtrude","SWEPT_BODY",BODY,{"disambiguationData":[OSD([sQuery(id+"F12.wireOp",EDGE,"E33.bottom"),sQuery(id+"F12.wireOp",EDGE,"E33.top"),sQuery(id+"F12.wireOp",EDGE,"E33.left"),sQuery(id+"F12.wireOp",EDGE,"E33.right"),sQuery(id+"F12.wireOp",EDGE,"E34.bottom"),sQuery(id+"F12.wireOp",EDGE,"E34.top"),sQuery(id+"F12.wireOp",EDGE,"E34.left"),sQuery(id+"F12.wireOp",EDGE,"E34.right")])]});
            var Q1;
            Q1=makeQuery(id+"F55.opExtrude","SWEPT_BODY",BODY,{"disambiguationData":[OSD([sQuery(id+"F54.wireOp",EDGE,"E82.bottom"),sQuery(id+"F54.wireOp",EDGE,"E82.top"),sQuery(id+"F54.wireOp",EDGE,"E82.left"),sQuery(id+"F54.wireOp",EDGE,"E82.right")])]});
            var Q2;
            Q2=makeQuery(id+"F45.opExtrude","SWEPT_BODY",BODY,{"disambiguationData":[OSD([sQuery(id+"F44.wireOp",EDGE,"E72.bottom"),sQuery(id+"F44.wireOp",EDGE,"E72.top"),sQuery(id+"F44.wireOp",EDGE,"E72.left"),sQuery(id+"F44.wireOp",EDGE,"E72.right")])]});
            var Q3;
            Q3=makeQuery(id+"F61.opPattern","COPY",BODY,{"derivedFrom":makeQuery(id+"F53.opExtrude","SWEPT_BODY",BODY,{"disambiguationData":[OSD([sQuery(id+"F52.wireOp",EDGE,"E81.bottom"),sQuery(id+"F52.wireOp",EDGE,"E81.top"),sQuery(id+"F52.wireOp",EDGE,"E81.left"),sQuery(id+"F52.wireOp",EDGE,"E81.right")])]}),"instanceName":"1"});
            var Q4;
            Q4=makeQuery(id+"F61.opPattern","COPY",BODY,{"derivedFrom":makeQuery(id+"F55.opExtrude","SWEPT_BODY",BODY,{"disambiguationData":[OSD([sQuery(id+"F54.wireOp",EDGE,"E82.bottom"),sQuery(id+"F54.wireOp",EDGE,"E82.top"),sQuery(id+"F54.wireOp",EDGE,"E82.left"),sQuery(id+"F54.wireOp",EDGE,"E82.right")])]}),"instanceName":"1"});
            var Q5;
            Q5=makeQuery(id+"F42.opExtrude","SWEPT_BODY",BODY,{"disambiguationData":[OSD([sQuery(id+"F41.wireOp",EDGE,"E69.bottom"),sQuery(id+"F41.wireOp",EDGE,"E69.top"),sQuery(id+"F41.wireOp",EDGE,"E69.left"),sQuery(id+"F41.wireOp",EDGE,"E69.right")])]});
            booleanBodies(context, id + "F64", {"operationType" : BooleanOperationType.SUBTRACTION, "tools" : qUnion([Q0]), "targets" : qUnion([Q1, Q2, Q3, Q4, Q5]), "keepTools" : true});
        }
        {
            var Q0;
            Q0=makeQuery(id+"F13.opExtrude","CAP_FACE",FACE,{"disambiguationData":[OSD([sQuery(id+"F12.wireOp",EDGE,"E33.bottom"),sQuery(id+"F12.wireOp",EDGE,"E33.top"),sQuery(id+"F12.wireOp",EDGE,"E33.left"),sQuery(id+"F12.wireOp",EDGE,"E33.right"),sQuery(id+"F12.wireOp",EDGE,"E34.bottom"),sQuery(id+"F12.wireOp",EDGE,"E34.top"),sQuery(id+"F12.wireOp",EDGE,"E34.left"),sQuery(id+"F12.wireOp",EDGE,"E34.right")])],"isStart":false});
            var sketch = newSketch(context, id + "F65", { "sketchPlane" : qUnion([Q0])});
            skLineSegment(sketch, "E87.bottom", {"start": v(1, 1000) * mm, "end": v(-1, 1000) * mm});
            skLineSegment(sketch, "E87.top", {"start": v(1, -1000) * mm, "end": v(-1, -1000) * mm});
            skLineSegment(sketch, "E87.left", {"start": v(1, 1000) * mm, "end": v(1, -1000) * mm});
            skLineSegment(sketch, "E87.right", {"start": v(-1, 1000) * mm, "end": v(-1, -1000) * mm});
            skPoint(sketch, "E87.middle", {"position": v(0, 0) * mm});
            skSolve(sketch);
        }
        {
            var Q0;
            Q0 = qSketchRegion(id + "F65", true);
            extrude(context, id + "F66", {"entities" : qUnion([Q0]), "oppositeDirection" : true, "depth" : 2648 * mm, "symmetric" : true});
        }
        {
            var Q0;
            Q0 = qSketchRegion(id + "F65", true);
            extrude(context, id + "F67", {"entities" : qUnion([Q0]), "depth" : 25 * mm});
        }
        {
            var Q0;
            Q0=makeQuery(id+"F66.opExtrude","SWEPT_BODY",BODY,{"disambiguationData":[OSD([sQuery(id+"F65.wireOp",EDGE,"E87.bottom"),sQuery(id+"F65.wireOp",EDGE,"E87.top"),sQuery(id+"F65.wireOp",EDGE,"E87.left"),sQuery(id+"F65.wireOp",EDGE,"E87.right")])]});
            var Q1;
            Q1=makeQuery(id+"F13.opExtrude","SWEPT_BODY",BODY,{"disambiguationData":[OSD([sQuery(id+"F12.wireOp",EDGE,"E33.bottom"),sQuery(id+"F12.wireOp",EDGE,"E33.top"),sQuery(id+"F12.wireOp",EDGE,"E33.left"),sQuery(id+"F12.wireOp",EDGE,"E33.right"),sQuery(id+"F12.wireOp",EDGE,"E34.bottom"),sQuery(id+"F12.wireOp",EDGE,"E34.top"),sQuery(id+"F12.wireOp",EDGE,"E34.left"),sQuery(id+"F12.wireOp",EDGE,"E34.right")])]});
            var Q2;
            Q2=makeQuery(id+"F5.opExtrude","SWEPT_BODY",BODY,{"disambiguationData":[OSD([sQuery(id+"F4.wireOp",EDGE,"E2.bottom"),sQuery(id+"F4.wireOp",EDGE,"E2.top"),sQuery(id+"F4.wireOp",EDGE,"E2.left"),sQuery(id+"F4.wireOp",EDGE,"E2.right")])]});
            var Q3;
            Q3=makeQuery(id+"F3.opExtrude","SWEPT_BODY",BODY,{"disambiguationData":[OSD([sQuery(id+"F2.wireOp",EDGE,"E1.bottom"),sQuery(id+"F2.wireOp",EDGE,"E1.top"),sQuery(id+"F2.wireOp",EDGE,"E1.left"),sQuery(id+"F2.wireOp",EDGE,"E1.right")])]});
            var Q4;
            Q4=makeQuery(id+"F1.opExtrude","SWEPT_BODY",BODY,{"disambiguationData":[OSD([sQuery(id+"F0.wireOp",EDGE,"E0.bottom"),sQuery(id+"F0.wireOp",EDGE,"E0.top"),sQuery(id+"F0.wireOp",EDGE,"E0.left"),sQuery(id+"F0.wireOp",EDGE,"E0.right")])]});
            var Q5;
            Q5=makeQuery(id+"F7.opExtrude","SWEPT_BODY",BODY,{"disambiguationData":[OSD([sQuery(id+"F6.wireOp",EDGE,"E3.bottom"),sQuery(id+"F6.wireOp",EDGE,"E3.top"),sQuery(id+"F6.wireOp",EDGE,"E3.left"),sQuery(id+"F6.wireOp",EDGE,"E3.right")])]});
            booleanBodies(context, id + "F68", {"operationType" : BooleanOperationType.SUBTRACTION, "tools" : qUnion([Q0]), "targets" : qUnion([Q1, Q2, Q3, Q4, Q5])});
        }
        {
            var Q0;
            Q0=makeQuery(id+"F67.opExtrude","SWEPT_BODY",BODY,{"disambiguationData":[OSD([sQuery(id+"F65.wireOp",EDGE,"E87.bottom"),sQuery(id+"F65.wireOp",EDGE,"E87.top"),sQuery(id+"F65.wireOp",EDGE,"E87.left"),sQuery(id+"F65.wireOp",EDGE,"E87.right")])]});
            deleteBodies(context, id + "F69", {"entities" : qUnion([Q0])});
        }
        {
            var Q0;
            Q0=makeQuery(id+"F9.opExtrude","CAP_FACE",FACE,{"disambiguationData":[OSD([sQuery(id+"F8.wireOp",EDGE,"E9"),sQuery(id+"F8.wireOp",EDGE,"E10"),sQuery(id+"F8.wireOp",EDGE,"E17.trimOffspring"),sQuery(id+"F8.wireOp",EDGE,"E21.trimOffspring")])],"isStart":false});
            var sketch = newSketch(context, id + "F70", { "sketchPlane" : qUnion([Q0])});
            skLineSegment(sketch, "E88", {"start": v(884.84, 0) * mm, "end": v(884.84, 30) * mm, "construction": true});
            skLineSegment(sketch, "E89", {"start": v(884.84, -530) * mm, "end": v(884.84, -560) * mm});
            skLineSegment(sketch, "E90.bottom", {"start": v(948.06, 30) * mm, "end": v(-62.87, 30) * mm});
            skLineSegment(sketch, "E90.top", {"start": v(948.06, -560) * mm, "end": v(-62.87, -560) * mm});
            skLineSegment(sketch, "E90.left", {"start": v(948.06, 30) * mm, "end": v(948.06, -560) * mm});
            skLineSegment(sketch, "E90.right", {"start": v(-62.87, 30) * mm, "end": v(-62.87, -560) * mm});
            skSolve(sketch);
        }
        {
            var Q0;
            Q0 = qSketchRegion(id + "F70", true);
            extrude(context, id + "F71", {"entities" : qUnion([Q0]), "operationType" : NewBodyOperationType.REMOVE, "oppositeDirection" : true, "depth" : 25 * mm});
        }
        {
            var Q0;
            Q0=makeQuery(id+"F11.opExtrude","SWEPT_FACE",FACE,{"disambiguationData":[OSD([sQuery(id+"F10.wireOp",EDGE,"E30.right")])]});
            var Q1;
            Q1=makeQuery(id+"F61.opPattern","COPY",FACE,{"derivedFrom":makeQuery(id+"F57.opExtrude","SWEPT_FACE",FACE,{"disambiguationData":[OSD([sQuery(id+"F56.wireOp",EDGE,"E83.left")])]}),"instanceName":"1"});
            shell(context, id + "F72", {"entities" : qUnion([Q0, Q1]), "thickness" : 20 * mm});
        }
        {
            var Q0;
            Q0=makeQuery(id+"F61.opPattern","COPY",FACE,{"derivedFrom":makeQuery(id+"F53.opExtrude","SWEPT_FACE",FACE,{"disambiguationData":[OSD([sQuery(id+"F52.wireOp",EDGE,"E81.right")])]}),"instanceName":"1"});
            shell(context, id + "F73", {"entities" : qUnion([Q0]), "thickness" : 20 * mm});
        }
        {
            var Q0;
            Q0=makeQuery(id+"F61.opPattern","COPY",FACE,{"derivedFrom":makeQuery(id+"F53.opExtrude","SWEPT_FACE",FACE,{"disambiguationData":[OSD([sQuery(id+"F52.wireOp",EDGE,"E81.right")])]}),"instanceName":"1"});
            var sketch = newSketch(context, id + "F74", { "sketchPlane" : qUnion([Q0])});
            skLineSegment(sketch, "E91.bottom", {"start": v(464.84, 1150) * mm, "end": v(884.84, 1150) * mm});
            skLineSegment(sketch, "E91.top", {"start": v(464.84, 730) * mm, "end": v(884.84, 730) * mm});
            skLineSegment(sketch, "E91.left", {"start": v(464.84, 1150) * mm, "end": v(464.84, 730) * mm});
            skLineSegment(sketch, "E91.right", {"start": v(884.84, 1150) * mm, "end": v(884.84, 730) * mm});
            skSolve(sketch);
        }
        {
            var Q0;
            Q0 = qSketchRegion(id + "F74", true);
            extrude(context, id + "F75", {"entities" : qUnion([Q0]), "oppositeDirection" : true, "depth" : 20 * mm});
        }
        {
            var Q0;
            Q0=makeQuery(id+"F61.opPattern","COPY",FACE,{"derivedFrom":makeQuery(id+"F57.opExtrude","SWEPT_FACE",FACE,{"disambiguationData":[OSD([sQuery(id+"F56.wireOp",EDGE,"E83.left")])]}),"instanceName":"1"});
            var sketch = newSketch(context, id + "F76", { "sketchPlane" : qUnion([Q0])});
            skLineSegment(sketch, "E92.bottom", {"start": v(-890, 1130) * mm, "end": v(-550, 1130) * mm});
            skLineSegment(sketch, "E92.top", {"start": v(-890, 730) * mm, "end": v(-550, 730) * mm});
            skLineSegment(sketch, "E92.left", {"start": v(-890, 1130) * mm, "end": v(-890, 730) * mm});
            skLineSegment(sketch, "E92.right", {"start": v(-550, 1130) * mm, "end": v(-550, 730) * mm});
            skSolve(sketch);
        }
        {
            var Q0;
            Q0 = qSketchRegion(id + "F76", true);
            extrude(context, id + "F77", {"entities" : qUnion([Q0]), "operationType" : NewBodyOperationType.ADD, "oppositeDirection" : true, "depth" : 20 * mm});
        }
        {
            var Q0;
            Q0=makeQuery(id+"F11.opExtrude","SWEPT_FACE",FACE,{"disambiguationData":[OSD([sQuery(id+"F10.wireOp",EDGE,"E30.right")])]});
            var sketch = newSketch(context, id + "F78", { "sketchPlane" : qUnion([Q0])});
            skLineSegment(sketch, "E93.bottom", {"start": v(-530, 700) * mm, "end": v(0, 700) * mm});
            skLineSegment(sketch, "E93.top", {"start": v(-530, 270) * mm, "end": v(0, 270) * mm});
            skLineSegment(sketch, "E93.left", {"start": v(-530, 700) * mm, "end": v(-530, 270) * mm});
            skLineSegment(sketch, "E93.right", {"start": v(0, 700) * mm, "end": v(0, 270) * mm});
            skSolve(sketch);
        }
        {
            var Q0;
            Q0 = qSketchRegion(id + "F78", true);
            extrude(context, id + "F79", {"entities" : qUnion([Q0]), "operationType" : NewBodyOperationType.ADD, "oppositeDirection" : true, "depth" : 20 * mm});
        }
        {
            var Q0;
            Q0=makeQuery(id+"F68.opBoolean","SPLIT",BODY,{"disambiguationData":[OD(0.0)],"derivedFrom":makeQuery(id+"F13.opExtrude","SWEPT_BODY",BODY,{"disambiguationData":[OSD([sQuery(id+"F12.wireOp",EDGE,"E33.bottom"),sQuery(id+"F12.wireOp",EDGE,"E33.top"),sQuery(id+"F12.wireOp",EDGE,"E33.left"),sQuery(id+"F12.wireOp",EDGE,"E33.right"),sQuery(id+"F12.wireOp",EDGE,"E34.bottom"),sQuery(id+"F12.wireOp",EDGE,"E34.top"),sQuery(id+"F12.wireOp",EDGE,"E34.left"),sQuery(id+"F12.wireOp",EDGE,"E34.right")])]})});
            var Q1;
            Q1=makeQuery(id+"F11.opExtrude","SWEPT_BODY",BODY,{"disambiguationData":[OSD([sQuery(id+"F10.wireOp",EDGE,"E28.bottom"),sQuery(id+"F10.wireOp",EDGE,"E28.top"),sQuery(id+"F10.wireOp",EDGE,"E28.left"),sQuery(id+"F10.wireOp",EDGE,"E28.right")])]});
            booleanBodies(context, id + "F80", {"operationType" : BooleanOperationType.SUBTRACTION, "tools" : qUnion([Q0]), "targets" : qUnion([Q1]), "keepTools" : true});
        }
        {
            var Q0;
            Q0=makeQuery(id+"F11.opExtrude","SWEPT_FACE",FACE,{"disambiguationData":[OSD([sQuery(id+"F10.wireOp",EDGE,"E28.left")])]});
            shell(context, id + "F81", {"entities" : qUnion([Q0]), "thickness" : 20 * mm});
        }
        {
            var Q0;
            Q0=makeQuery(id+"F11.opExtrude","SWEPT_FACE",FACE,{"disambiguationData":[OSD([sQuery(id+"F10.wireOp",EDGE,"E28.left")])]});
            var sketch = newSketch(context, id + "F82", { "sketchPlane" : qUnion([Q0])});
            skLineSegment(sketch, "E94.bottom", {"start": v(100, 700) * mm, "end": v(-500, 700) * mm});
            skLineSegment(sketch, "E94.top", {"start": v(100, 270) * mm, "end": v(-500, 270) * mm});
            skLineSegment(sketch, "E94.left", {"start": v(100, 700) * mm, "end": v(100, 270) * mm});
            skLineSegment(sketch, "E94.right", {"start": v(-500, 700) * mm, "end": v(-500, 270) * mm});
            skSolve(sketch);
        }
        {
            var Q0;
            Q0 = qSketchRegion(id + "F82", true);
            extrude(context, id + "F83", {"entities" : qUnion([Q0]), "operationType" : NewBodyOperationType.ADD, "oppositeDirection" : true, "depth" : 20 * mm});
        }
        {
            var Q0;
            Q0=makeQuery(id+"F68.opBoolean","SPLIT",BODY,{"disambiguationData":[OD(0.0)],"derivedFrom":makeQuery(id+"F13.opExtrude","SWEPT_BODY",BODY,{"disambiguationData":[OSD([sQuery(id+"F12.wireOp",EDGE,"E33.bottom"),sQuery(id+"F12.wireOp",EDGE,"E33.top"),sQuery(id+"F12.wireOp",EDGE,"E33.left"),sQuery(id+"F12.wireOp",EDGE,"E33.right"),sQuery(id+"F12.wireOp",EDGE,"E34.bottom"),sQuery(id+"F12.wireOp",EDGE,"E34.top"),sQuery(id+"F12.wireOp",EDGE,"E34.left"),sQuery(id+"F12.wireOp",EDGE,"E34.right")])]})});
            var Q1;
            Q1=makeQuery(id+"F11.opExtrude","SWEPT_BODY",BODY,{"disambiguationData":[OSD([sQuery(id+"F10.wireOp",EDGE,"E24.bottom"),sQuery(id+"F10.wireOp",EDGE,"E24.top"),sQuery(id+"F10.wireOp",EDGE,"E24.left"),sQuery(id+"F10.wireOp",EDGE,"E24.right")])]});
            booleanBodies(context, id + "F84", {"operationType" : BooleanOperationType.SUBTRACTION, "tools" : qUnion([Q0]), "targets" : qUnion([Q1]), "keepTools" : true});
        }
    });
